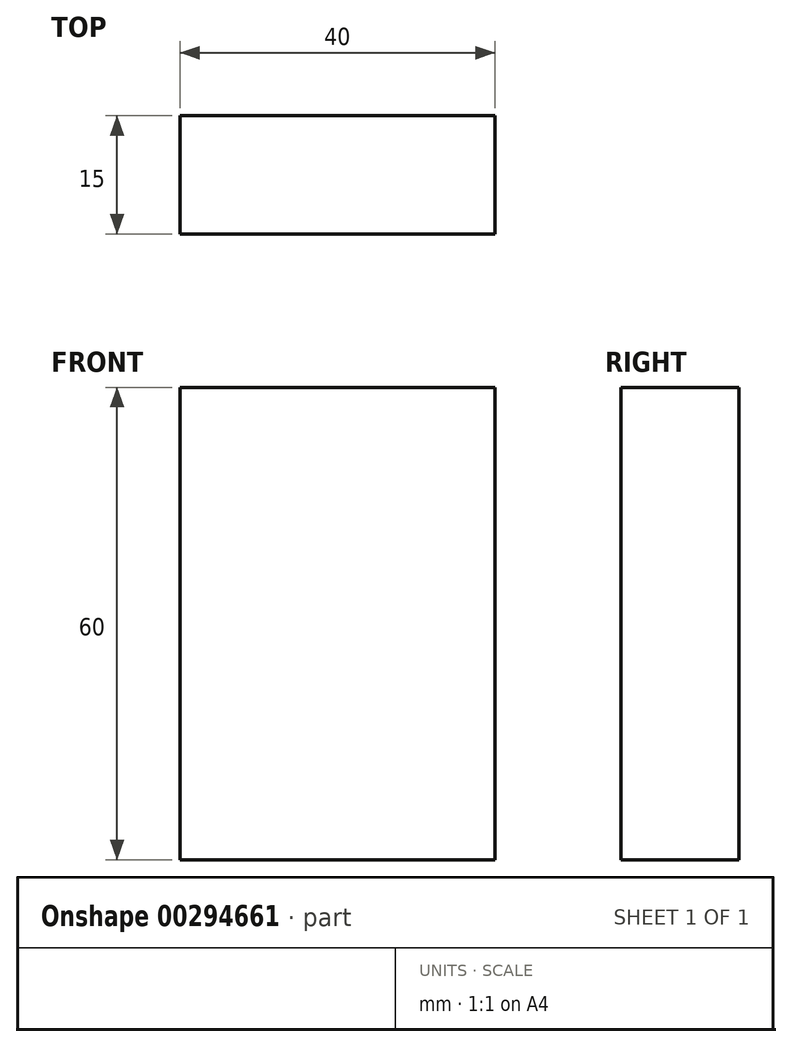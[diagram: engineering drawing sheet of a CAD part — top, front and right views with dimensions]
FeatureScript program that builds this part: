
annotation { "Feature Type Name" : "Feature", "Feature Type Description" : "" }
export const myFeature = defineFeature(function(context is Context, id is Id, definition is map)
    precondition{}
    {
        {
            var Q0;
            Q0=qCreatedBy(makeId("Front.planeOp"),FACE);
            var sketch = newSketch(context, id + "F0", { "sketchPlane" : qUnion([Q0])});
            skLineSegment(sketch, "E0.bottom", {"start": v(-20, 30) * mm, "end": v(20, 30) * mm});
            skLineSegment(sketch, "E0.top", {"start": v(-20, -30) * mm, "end": v(20, -30) * mm});
            skLineSegment(sketch, "E0.left", {"start": v(-20, 30) * mm, "end": v(-20, -30) * mm});
            skLineSegment(sketch, "E0.right", {"start": v(20, 30) * mm, "end": v(20, -30) * mm});
            skPoint(sketch, "E0.middle", {"position": v(0, 0) * mm});
            skSolve(sketch);
        }
        {
            var Q0;
            Q0 = qSketchRegion(id + "F0", true);
            extrude(context, id + "F1", {"entities" : qUnion([Q0]), "depth" : 15 * mm});
        }
    });
